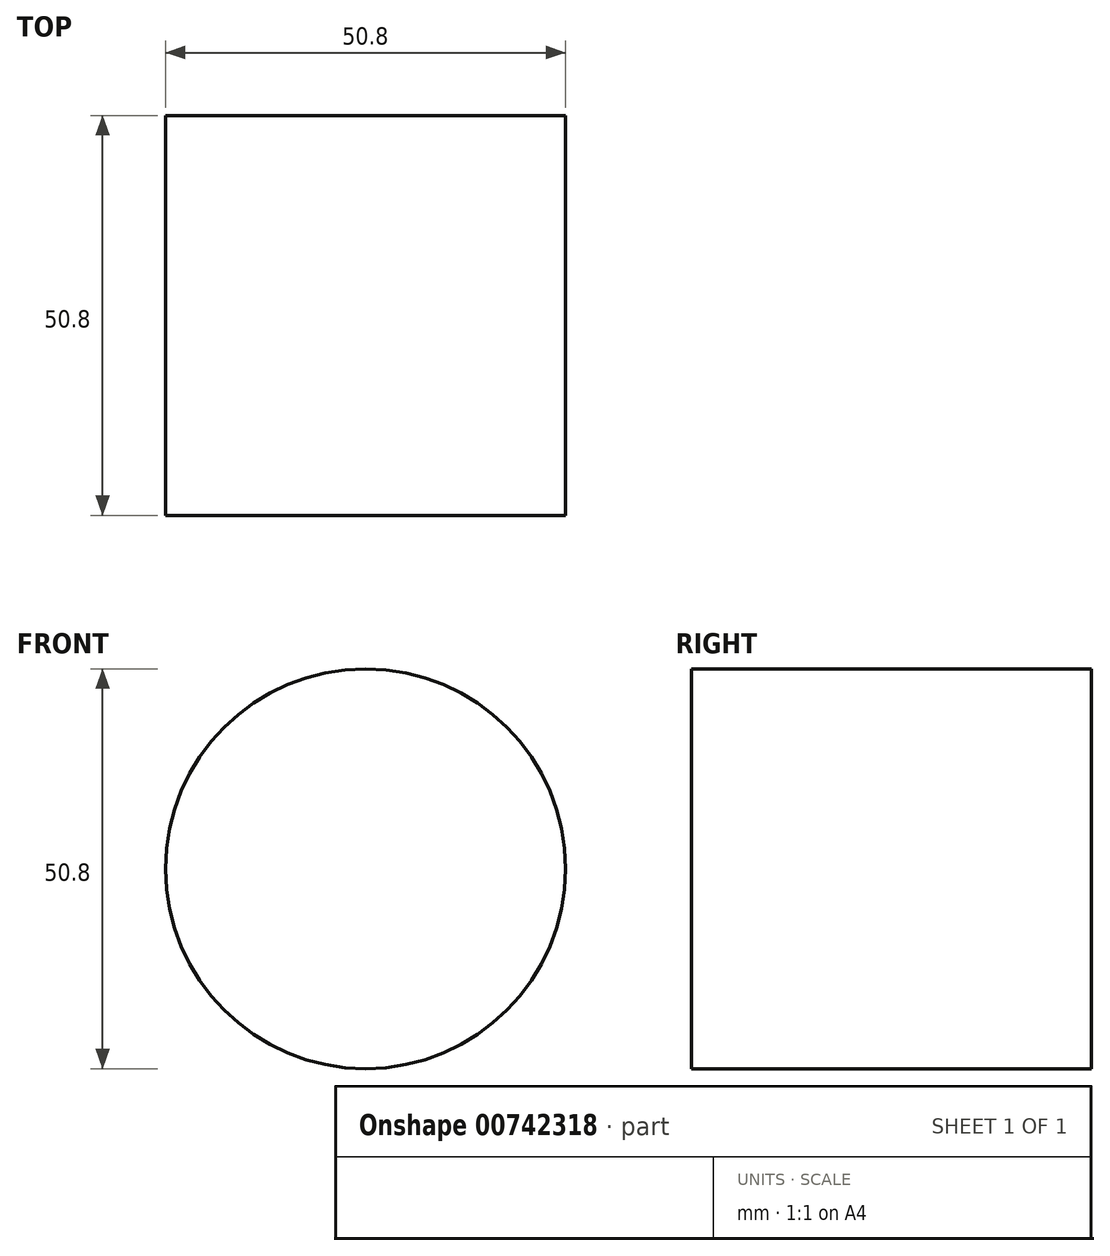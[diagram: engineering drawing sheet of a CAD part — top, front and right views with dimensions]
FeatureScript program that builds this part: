
annotation { "Feature Type Name" : "Feature", "Feature Type Description" : "" }
export const myFeature = defineFeature(function(context is Context, id is Id, definition is map)
    precondition{}
    {
        {
            var Q0;
            Q0=qCreatedBy(makeId("Front.planeOp"),FACE);
            var sketch = newSketch(context, id + "F0", { "sketchPlane" : qUnion([Q0])});
            skCircle(sketch, "E0", {"center": v(0, 0) * mm, "radius": 25.4 * mm});
            skSolve(sketch);
        }
        {
            var Q0;
            Q0=qSketchRegion(id+"F0",true);
            extrude(context, id + "F1", {"entities" : qUnion([Q0]), "endBound" : BoundingType.SYMMETRIC, "depth" : 50.8 * mm, "offsetDistance" : 25.4 * mm});
        }
    });
